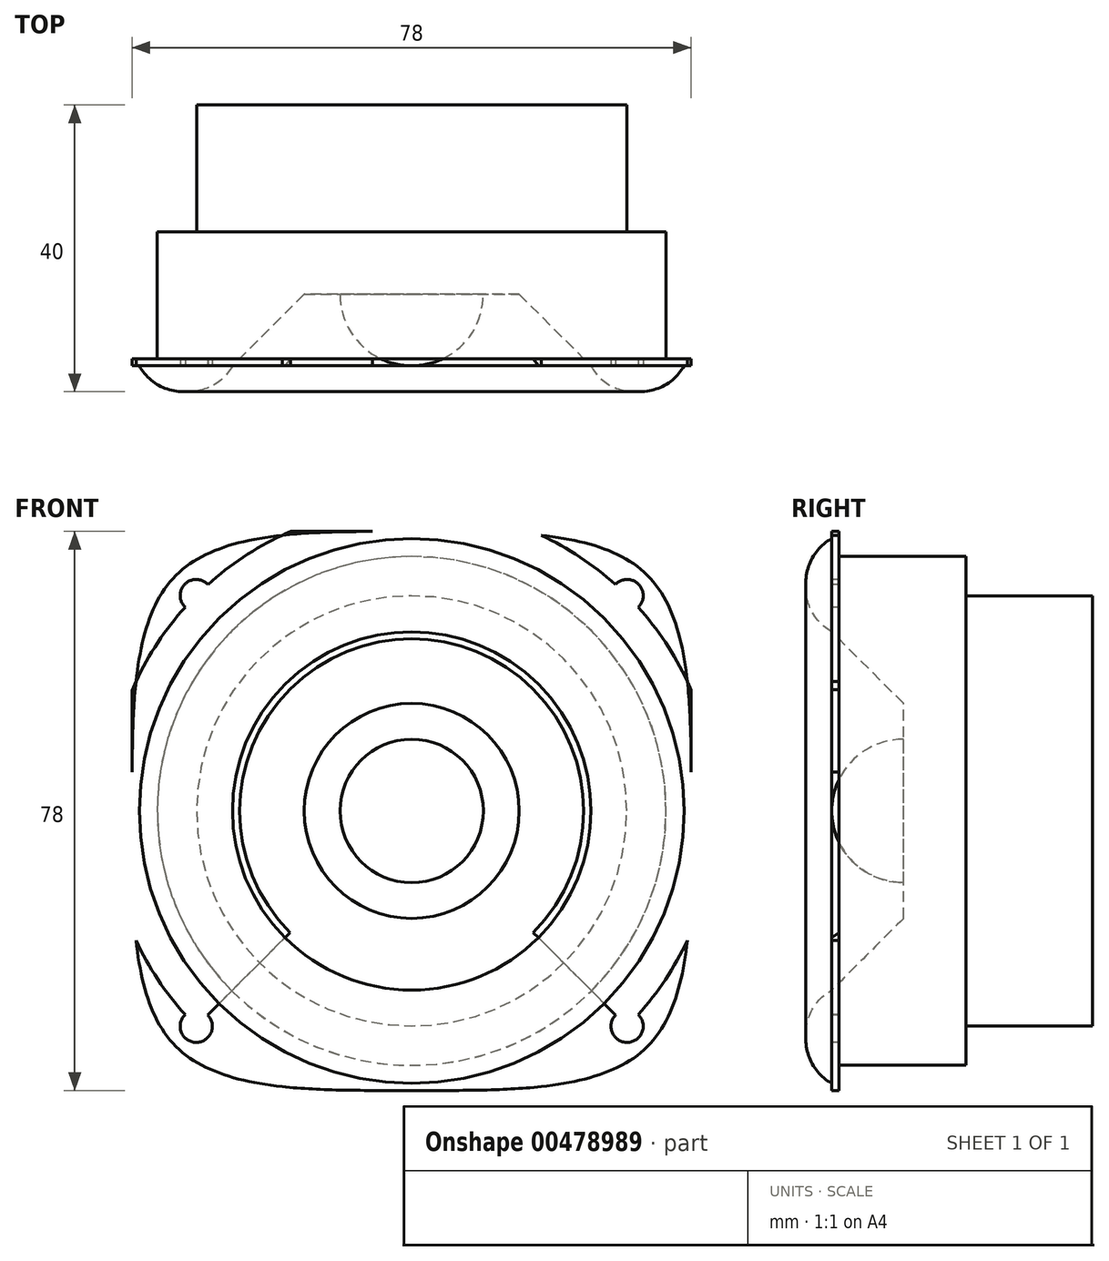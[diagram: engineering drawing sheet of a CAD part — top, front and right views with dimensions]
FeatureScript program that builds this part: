
annotation { "Feature Type Name" : "Feature", "Feature Type Description" : "" }
export const myFeature = defineFeature(function(context is Context, id is Id, definition is map)
    precondition{}
    {
        {
            var Q0;
            Q0=qCreatedBy(makeId("Front.planeOp"),FACE);
            var sketch = newSketch(context, id + "F0", { "sketchPlane" : qUnion([Q0])});
            skLineSegment(sketch, "E0.bottom", {"start": v(39, -39) * mm, "end": v(-39, -39) * mm});
            skLineSegment(sketch, "E0.top", {"start": v(39, 39) * mm, "end": v(-39, 39) * mm});
            skLineSegment(sketch, "E0.left", {"start": v(39, -39) * mm, "end": v(39, 39) * mm});
            skLineSegment(sketch, "E0.right", {"start": v(-39, -39) * mm, "end": v(-39, 39) * mm});
            skPoint(sketch, "E0.middle", {"position": v(0, 0) * mm});
            skLineSegment(sketch, "E1", {"start": v(-39, 39) * mm, "end": v(39, -39) * mm});
            skLineSegment(sketch, "E2", {"start": v(39, 39) * mm, "end": v(-39, -39) * mm});
            skCircle(sketch, "E3", {"center": v(0, 0) * mm, "radius": 46.5 * mm});
            skFitSpline(sketch, "E4", {"points": [v(0, 39) * mm, v(32.88, 32.88) * mm, v(39, 0) * mm, v(32.88, -32.88) * mm, v(0, -39) * mm, v(-32.88, -32.88) * mm, v(-39, 0) * mm, v(-32.88, 32.88) * mm, v(0, 39) * mm]});
            skCircle(sketch, "E5", {"center": v(0, 0) * mm, "radius": 42.5 * mm});
            skCircle(sketch, "E6", {"center": v(-30.05, 30.05) * mm, "radius": 2.25 * mm});
            skCircle(sketch, "E7", {"center": v(30.05, 30.05) * mm, "radius": 2.25 * mm});
            skCircle(sketch, "E8", {"center": v(30.05, -30.05) * mm, "radius": 2.25 * mm});
            skCircle(sketch, "E9", {"center": v(-30.05, -30.05) * mm, "radius": 2.25 * mm});
            skSolve(sketch);
        }
        {
            var Q0;
            {var subQ3=sQuery(id+"F0.wireOp",EDGE,"E4");var subQ5=sQuery(id+"F0.wireOp",EDGE,"E5");var subQ6=makeQuery(id+"F0.imprint","INTERSECT",VERTEX,{"disambiguationData":[OD(6.0)],"derivedFrom":[subQ3,subQ5]});Q0=makeQuery(id+"F0.imprint","IMPRINT",FACE,{"disambiguationData":[TD([[makeQuery(id+"F0.imprint","IMPRINT",EDGE,{"disambiguationData":[TD([[subQ6,1.0]])],"derivedFrom":subQ5}),-1.0]])]});}
            var Q1;
            {var subQ3=sQuery(id+"F0.wireOp",EDGE,"E4");var subQ5=sQuery(id+"F0.wireOp",EDGE,"E5");var subQ6=makeQuery(id+"F0.imprint","INTERSECT",VERTEX,{"disambiguationData":[OD(7.0)],"derivedFrom":[subQ3,subQ5]});Q1=makeQuery(id+"F0.imprint","IMPRINT",FACE,{"disambiguationData":[TD([[makeQuery(id+"F0.imprint","IMPRINT",EDGE,{"disambiguationData":[TD([[subQ6,-1.0]])],"derivedFrom":subQ5}),-1.0]])]});}
            var Q2;
            {var subQ7=sQuery(id+"F0.wireOp",EDGE,"E4");var subQ8=sQuery(id+"F0.wireOp",EDGE,"E0.right");var subQ9=makeQuery(id+"F0.imprint","INTERSECT",VERTEX,{"disambiguationData":[OD(0.0)],"derivedFrom":[subQ8,subQ7]});Q2=makeQuery(id+"F0.imprint","IMPRINT",FACE,{"disambiguationData":[TD([[makeQuery(id+"F0.imprint","IMPRINT",EDGE,{"disambiguationData":[TD([[subQ9,-1.0]])],"derivedFrom":subQ8}),-1.0]])]});}
            var Q3;
            {var subQ0=sQuery(id+"F0.wireOp",EDGE,"E4");var subQ1=sQuery(id+"F0.wireOp",EDGE,"E0.top");var subQ11=makeQuery(id+"F0.imprint","INTERSECT",VERTEX,{"disambiguationData":[OD(0.0)],"derivedFrom":[subQ1,subQ0]});Q3=makeQuery(id+"F0.imprint","IMPRINT",FACE,{"disambiguationData":[TD([[makeQuery(id+"F0.imprint","IMPRINT",EDGE,{"disambiguationData":[TD([[subQ11,-1.0]])],"derivedFrom":subQ1}),1.0]])]});}
            var Q4;
            {var subQ5=sQuery(id+"F0.wireOp",EDGE,"E4");var subQ6=sQuery(id+"F0.wireOp",EDGE,"E0.left");var subQ13=makeQuery(id+"F0.imprint","INTERSECT",VERTEX,{"disambiguationData":[OD(0.0)],"derivedFrom":[subQ6,subQ5]});Q4=makeQuery(id+"F0.imprint","IMPRINT",FACE,{"disambiguationData":[TD([[makeQuery(id+"F0.imprint","IMPRINT",EDGE,{"disambiguationData":[TD([[subQ13,-1.0]])],"derivedFrom":subQ6}),1.0]])]});}
            var Q5;
            {var subQ5=sQuery(id+"F0.wireOp",EDGE,"E4");var subQ6=sQuery(id+"F0.wireOp",EDGE,"E0.bottom");var subQ7=makeQuery(id+"F0.imprint","INTERSECT",VERTEX,{"disambiguationData":[OD(0.0)],"derivedFrom":[subQ6,subQ5]});Q5=makeQuery(id+"F0.imprint","IMPRINT",FACE,{"disambiguationData":[TD([[makeQuery(id+"F0.imprint","IMPRINT",EDGE,{"disambiguationData":[TD([[subQ7,-1.0]])],"derivedFrom":subQ6}),-1.0]])]});}
            var Q6;
            {var subQ3=sQuery(id+"F0.wireOp",EDGE,"E4");var subQ5=sQuery(id+"F0.wireOp",EDGE,"E5");var subQ6=makeQuery(id+"F0.imprint","INTERSECT",VERTEX,{"disambiguationData":[OD(3.0)],"derivedFrom":[subQ3,subQ5]});Q6=makeQuery(id+"F0.imprint","IMPRINT",FACE,{"disambiguationData":[TD([[makeQuery(id+"F0.imprint","IMPRINT",EDGE,{"disambiguationData":[TD([[subQ6,-1.0]])],"derivedFrom":subQ5}),-1.0]])]});}
            var Q7;
            {var subQ3=sQuery(id+"F0.wireOp",EDGE,"E4");var subQ5=sQuery(id+"F0.wireOp",EDGE,"E5");var subQ6=makeQuery(id+"F0.imprint","INTERSECT",VERTEX,{"disambiguationData":[OD(2.0)],"derivedFrom":[subQ3,subQ5]});Q7=makeQuery(id+"F0.imprint","IMPRINT",FACE,{"disambiguationData":[TD([[makeQuery(id+"F0.imprint","IMPRINT",EDGE,{"disambiguationData":[TD([[subQ6,1.0]])],"derivedFrom":subQ5}),-1.0]])]});}
            var Q8;
            {var subQ3=sQuery(id+"F0.wireOp",EDGE,"E4");var subQ5=sQuery(id+"F0.wireOp",EDGE,"E5");var subQ7=makeQuery(id+"F0.imprint","INTERSECT",VERTEX,{"disambiguationData":[OD(4.0)],"derivedFrom":[subQ3,subQ5]});Q8=makeQuery(id+"F0.imprint","IMPRINT",FACE,{"disambiguationData":[TD([[makeQuery(id+"F0.imprint","IMPRINT",EDGE,{"disambiguationData":[TD([[subQ7,1.0]])],"derivedFrom":subQ5}),-1.0]])]});}
            var Q9;
            {var subQ3=sQuery(id+"F0.wireOp",EDGE,"E4");var subQ5=sQuery(id+"F0.wireOp",EDGE,"E5");var subQ6=makeQuery(id+"F0.imprint","INTERSECT",VERTEX,{"disambiguationData":[OD(5.0)],"derivedFrom":[subQ3,subQ5]});Q9=makeQuery(id+"F0.imprint","IMPRINT",FACE,{"disambiguationData":[TD([[makeQuery(id+"F0.imprint","IMPRINT",EDGE,{"disambiguationData":[TD([[subQ6,-1.0]])],"derivedFrom":subQ5}),-1.0]])]});}
            var Q10;
            {var subQ3=sQuery(id+"F0.wireOp",EDGE,"E4");var subQ5=sQuery(id+"F0.wireOp",EDGE,"E5");var subQ6=makeQuery(id+"F0.imprint","INTERSECT",VERTEX,{"disambiguationData":[OD(0.0)],"derivedFrom":[subQ3,subQ5]});Q10=makeQuery(id+"F0.imprint","IMPRINT",FACE,{"disambiguationData":[TD([[makeQuery(id+"F0.imprint","IMPRINT",EDGE,{"disambiguationData":[TD([[subQ6,1.0]])],"derivedFrom":subQ5}),-1.0]])]});}
            var Q11;
            {var subQ3=sQuery(id+"F0.wireOp",EDGE,"E4");var subQ5=sQuery(id+"F0.wireOp",EDGE,"E5");var subQ7=makeQuery(id+"F0.imprint","INTERSECT",VERTEX,{"disambiguationData":[OD(1.0)],"derivedFrom":[subQ3,subQ5]});Q11=makeQuery(id+"F0.imprint","IMPRINT",FACE,{"disambiguationData":[TD([[makeQuery(id+"F0.imprint","IMPRINT",EDGE,{"disambiguationData":[TD([[subQ7,-1.0]])],"derivedFrom":subQ5}),-1.0]])]});}
            extrude(context, id + "F1", {"entities" : qUnion([Q0, Q1, Q2, Q3, Q4, Q5, Q6, Q7, Q8, Q9, Q10, Q11]), "oppositeDirection" : true, "depth" : 1 * mm});
        }
        {
            var Q0;
            Q0=makeQuery(id+"F1.opExtrude","CAP_FACE",FACE,{"disambiguationData":[OSD([sQuery(id+"F0.wireOp",EDGE,"E0.bottom"),sQuery(id+"F0.wireOp",EDGE,"E0.top"),sQuery(id+"F0.wireOp",EDGE,"E0.left"),sQuery(id+"F0.wireOp",EDGE,"E0.right"),sQuery(id+"F0.wireOp",EDGE,"E4"),sQuery(id+"F0.wireOp",EDGE,"E6"),sQuery(id+"F0.wireOp",EDGE,"E7"),sQuery(id+"F0.wireOp",EDGE,"E8"),sQuery(id+"F0.wireOp",EDGE,"E9")])],"isStart":false});
            var sketch = newSketch(context, id + "F2", { "sketchPlane" : qUnion([Q0])});
            skCircle(sketch, "E10", {"center": v(0, 0) * mm, "radius": 35.5 * mm});
            skSolve(sketch);
        }
        {
            var Q0;
            Q0 = qSketchRegion(id + "F2", true);
            extrude(context, id + "F3", {"entities" : qUnion([Q0]), "operationType" : NewBodyOperationType.ADD, "depth" : ((40 - 4.6) / 2) * mm});
        }
        {
            var Q0;
            Q0=makeQuery(id+"F3.opExtrude","CAP_FACE",FACE,{"disambiguationData":[OSD([sQuery(id+"F2.wireOp",EDGE,"E10")])],"isStart":false});
            var sketch = newSketch(context, id + "F4", { "sketchPlane" : qUnion([Q0])});
            skCircle(sketch, "E11", {"center": v(0, 0) * mm, "radius": 30 * mm});
            skSolve(sketch);
        }
        {
            var Q0;
            Q0 = qSketchRegion(id + "F4", true);
            extrude(context, id + "F5", {"entities" : qUnion([Q0]), "operationType" : NewBodyOperationType.ADD, "depth" : ((40 - 4.6) / 2) * mm});
        }
        {
            var Q0;
            Q0=makeQuery(id+"F1.opExtrude","CAP_FACE",FACE,{"disambiguationData":[OSD([sQuery(id+"F0.wireOp",EDGE,"E0.bottom"),sQuery(id+"F0.wireOp",EDGE,"E0.top"),sQuery(id+"F0.wireOp",EDGE,"E0.left"),sQuery(id+"F0.wireOp",EDGE,"E0.right"),sQuery(id+"F0.wireOp",EDGE,"E4"),sQuery(id+"F0.wireOp",EDGE,"E6"),sQuery(id+"F0.wireOp",EDGE,"E7"),sQuery(id+"F0.wireOp",EDGE,"E8"),sQuery(id+"F0.wireOp",EDGE,"E9")])],"isStart":true});
            var sketch = newSketch(context, id + "F6", { "sketchPlane" : qUnion([Q0])});
            skCircle(sketch, "E12", {"center": v(0, 0) * mm, "radius": 25 * mm});
            skSolve(sketch);
        }
        {
            var Q0;
            Q0 = qSketchRegion(id + "F6", true);
            extrude(context, id + "F7", {"entities" : qUnion([Q0]), "operationType" : NewBodyOperationType.REMOVE, "oppositeDirection" : true, "depth" : 10 * mm});
        }
        {
            var Q0;
            Q0=makeQuery(id+"F7.boolean.opBoolean","COPY",FACE,{"derivedFrom":makeQuery(id+"F7.opExtrude","CAP_FACE",FACE,{"disambiguationData":[OSD([sQuery(id+"F6.wireOp",EDGE,"E12")])],"isStart":false})});
            var sketch = newSketch(context, id + "F8", { "sketchPlane" : qUnion([Q0])});
            skCircle(sketch, "E13", {"center": v(0, 0) * mm, "radius": 10 * mm});
            skSolve(sketch);
        }
        {
            var Q0;
            Q0 = qSketchRegion(id + "F8", true);
            extrude(context, id + "F9", {"entities" : qUnion([Q0]), "operationType" : NewBodyOperationType.ADD, "depth" : 10 * mm});
        }
        {
            var Q0;
            Q0=makeQuery(id+"F9.opExtrude","CAP_EDGE",EDGE,{"disambiguationData":[OSD([sQuery(id+"F8.wireOp",EDGE,"E13")])],"isStart":false});
            fillet(context, id + "F10", {"entities" : qUnion([Q0]), "radius" : 10 * mm, "tangentPropagation" : true, "allowEdgeOverflow" : false});
        }
        {
            var Q0;
            Q0=makeQuery(id+"F1.opExtrude","CAP_FACE",FACE,{"disambiguationData":[OSD([sQuery(id+"F0.wireOp",EDGE,"E0.bottom"),sQuery(id+"F0.wireOp",EDGE,"E0.top"),sQuery(id+"F0.wireOp",EDGE,"E0.left"),sQuery(id+"F0.wireOp",EDGE,"E0.right"),sQuery(id+"F0.wireOp",EDGE,"E4"),sQuery(id+"F0.wireOp",EDGE,"E6"),sQuery(id+"F0.wireOp",EDGE,"E7"),sQuery(id+"F0.wireOp",EDGE,"E8"),sQuery(id+"F0.wireOp",EDGE,"E9")])],"isStart":true});
            var sketch = newSketch(context, id + "F11", { "sketchPlane" : qUnion([Q0])});
            skCircle(sketch, "E14", {"center": v(0, 0) * mm, "radius": 38 * mm});
            skCircle(sketch, "E15", {"center": v(0, 0) * mm, "radius": 25 * mm});
            skSolve(sketch);
        }
        {
            var Q0;
            Q0 = qSketchRegion(id + "F11", true);
            extrude(context, id + "F12", {"entities" : qUnion([Q0]), "operationType" : NewBodyOperationType.ADD, "depth" : 3.6 * mm});
        }
        {
            var Q0;
            Q0=makeQuery(id+"F7.boolean.opBoolean","COPY",EDGE,{"derivedFrom":makeQuery(id+"F7.opExtrude","CAP_EDGE",EDGE,{"disambiguationData":[OSD([sQuery(id+"F6.wireOp",EDGE,"E12")])],"isStart":false})});
            chamfer(context, id + "F13", {"entities" : qUnion([Q0]), "width" : 10 * mm, "tangentPropagation" : true});
        }
        {
            var Q0;
            Q0=makeQuery(id+"F12.opExtrude","CAP_EDGE",EDGE,{"disambiguationData":[OSD([sQuery(id+"F11.wireOp",EDGE,"E14")])],"isStart":false});
            var Q1;
            Q1=makeQuery(id+"F12.opExtrude","CAP_EDGE",EDGE,{"disambiguationData":[OSD([sQuery(id+"F11.wireOp",EDGE,"E15")])],"isStart":false});
            fillet(context, id + "F14", {"entities" : qUnion([Q0, Q1]), "radius" : 7 * mm, "tangentPropagation" : true, "allowEdgeOverflow" : false});
        }
    });
